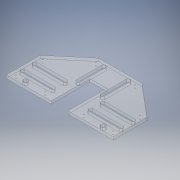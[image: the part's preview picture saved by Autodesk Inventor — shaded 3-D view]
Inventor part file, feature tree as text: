
AUTODESK INVENTOR PART (.ipt)
format: ipt  version: 2019 (Build 230136000, 136)  size: 256,512 bytes
history: native  units: mm
features: extrude x1
ambient origin geometry x8: Origin, YZ Plane, XZ Plane, XY Plane, X Axis, Y Axis, Z Axis, Center Point
bodies: Body1 (feature_tree)
feature tree (1):
  extrude  "Extrusion2"  Depth=6.0mm TaperAngle=0.0deg
